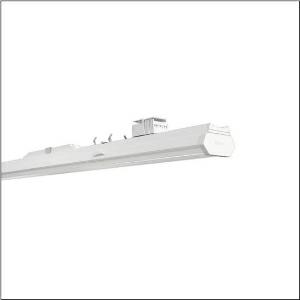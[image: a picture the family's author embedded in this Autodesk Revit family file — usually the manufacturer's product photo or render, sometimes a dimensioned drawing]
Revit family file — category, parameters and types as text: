
# Revit family: licross_r__11_protected_ho_51ts12cn4c5ld_3b37
name_source: partatom
category: Lighting Fixtures
units: mm (PartAtom-declared; Revit-internal decimal feet)

## family parameters
Cut with Voids When Loaded = No
Host = Face
Light Source = No
Part Type = Normal
Room Calculation Point = No
Round Connector Dimension = Use Diameter
Shared = No

## types (1)
- --- (1 x LED, 3110 lm, 21.7 W, 4000K)
    Apparent Load = 22 VA
    CIE Flux Codes = 54 82 95 97 100
    Color Rendering = 80
    Color Temperature = 4000K
    Default Elevation = 1800 mm
    Description = Licross® 11 Protected HOluminaire insert, length: 1.500mm, width: 90mm, height: 101mm, LED rated luminous flux: 12.600lm, light colour: 840, control gear: ON/OFF Multilumen, CLOi, control gear: ECG Multilumen, with plug, 6-pole, with phase selection, mains connection: 220..240V, AC/DC, 0/50..60Hz, without changeover relay, for emergency light function, for central battery installations according to DIN EN 60598-2-22, halogen-free wiring, primary optical cover: cover, of PMMA, light emission: direct with ceiling illumination distribution, protection rating (complete): IP50, insulation class (complete): insulation class I (protective earthing), certification: CE, ENEC, VDE, protection symbol: D if used in an environment without relevant dust loads with corresponding accessories, permissible ambient temperature for indoor applications: -35..+40°C, standard: EN 60598-2-22, reducing of maximum allowable ambient temperature of 5°C with ceiling mounting, corresponds to IFS (International Featured Standards) requirements for safety and quality in the food industry, packaging unit: 1 piece
    Height = 92 mm
    Lamp = 1 x LED
    Lamp Light Flux = 3110 lm
    Lamp Power = 21.7 W
    Lamp count = 1
    Length = 1500 mm
    Luminous efficacy = 143 lm/W
    Manufacturer = Siteco
    ModVariant = No
    Model = 51TS12CN4C5LD
    Mounting Place = Ceiling
    Mounting Type = Pendant
    Number of Poles = 1
    OnlyDefault = Yes
    Power Factor = 1
    Product Name = Licross® 11 Protected HO
    Product group = luminaire insert
    ProductGroupID = 902
    Protection Class = Protection class I
    Protection Degree = IP 50
    RLX_Detail_Level = 1
    RlxData = <blob elided: 22197 chars, md5=05cf4528>
    Socket = socket
    Standby Power = 0 W
    System Light Flux = 3110 lm
    System Power = 22 W
    Type Comments = : DC mode (central or group accumulator) initial emergency light level
    Type Image = l_1256145.jpg
    URL = http://relux.com
    VarID = @adj_134887
    Voltage = 0 V
    Weight = 0.00 kg
    Width = 88 mm

## geometry (parser evidence)
native form markers: Blend x4, Sweep x10
no freeform markers — native parametric forms only
